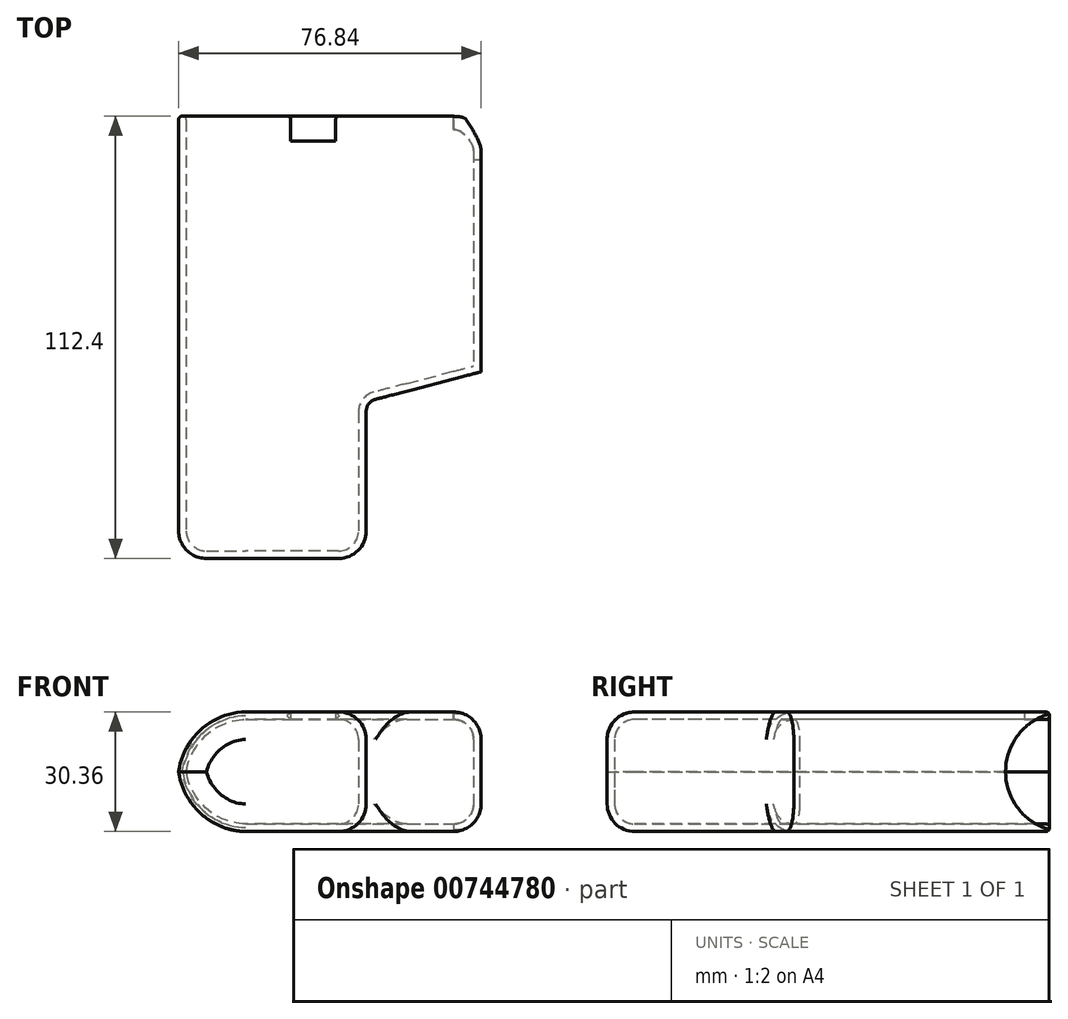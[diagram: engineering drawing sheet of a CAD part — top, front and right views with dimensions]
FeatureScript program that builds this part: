
annotation { "Feature Type Name" : "Feature", "Feature Type Description" : "" }
export const myFeature = defineFeature(function(context is Context, id is Id, definition is map)
    precondition{}
    {
        {
            var Q0;
            Q0=qCreatedBy(makeId("Top.planeOp"),FACE);
            var sketch = newSketch(context, id + "F0", { "sketchPlane" : qUnion([Q0])});
            skLineSegment(sketch, "E0", {"start": v(-37.72, -82.37) * mm, "end": v(-37.72, 28.12) * mm});
            skLineSegment(sketch, "E1", {"start": v(35.43, 28.12) * mm, "end": v(35.43, -35.38) * mm});
            skLineSegment(sketch, "E2", {"start": v(6.22, -43) * mm, "end": v(6.22, -82.37) * mm});
            skLineSegment(sketch, "E3", {"start": v(6.22, -82.37) * mm, "end": v(-37.72, -82.37) * mm});
            skLineSegment(sketch, "E4", {"start": v(-37.72, 28.12) * mm, "end": v(35.43, 28.12) * mm});
            skLineSegment(sketch, "E5", {"start": v(6.22, -43) * mm, "end": v(35.43, -35.38) * mm});
            skSolve(sketch);
        }
        {
            var Q0;
            Q0=makeQuery(id+"F0.imprint","IMPRINT",FACE,{"disambiguationData":[TD([[makeQuery(id+"F0.imprint","IMPRINT",EDGE,{"derivedFrom":sQuery(id+"F0.wireOp",EDGE,"E0")}),-1.0]])]});
            extrude(context, id + "F1", {"entities" : qUnion([Q0]), "endBound" : BoundingType.SYMMETRIC, "depth" : 26.54 * mm, "offsetDistance" : 25.4 * mm});
        }
        {
            var Q0;
            Q0=makeQuery(id+"F1.opExtrude","CAP_EDGE",EDGE,{"disambiguationData":[OSD([sQuery(id+"F0.wireOp",EDGE,"E0")])],"isStart":false});
            var Q1;
            Q1=makeQuery(id+"F1.opExtrude","CAP_EDGE",EDGE,{"disambiguationData":[OSD([sQuery(id+"F0.wireOp",EDGE,"E0")])],"isStart":true});
            fillet(context, id + "F2", {"entities" : qUnion([Q0, Q1]), "radius" : 15.24 * mm, "tangentPropagation" : true, "rho" : .4, "crossSection" : FilletCrossSection.CONIC, "allowEdgeOverflow" : false});
        }
        {
            var Q0;
            Q0=makeQuery(id+"F1.opExtrude","SWEPT_FACE",FACE,{"disambiguationData":[OSD([sQuery(id+"F0.wireOp",EDGE,"E3")])]});
            var Q1;
            Q1=makeQuery(id+"F1.opExtrude","SWEPT_FACE",FACE,{"disambiguationData":[OSD([sQuery(id+"F0.wireOp",EDGE,"E2")])]});
            var Q2;
            Q2=makeQuery(id+"F1.opExtrude","CAP_EDGE",EDGE,{"disambiguationData":[OSD([sQuery(id+"F0.wireOp",EDGE,"E1")])],"isStart":true});
            var Q3;
            Q3=makeQuery(id+"F1.opExtrude","CAP_EDGE",EDGE,{"disambiguationData":[OSD([sQuery(id+"F0.wireOp",EDGE,"E1")])],"isStart":false});
            fillet(context, id + "F3", {"entities" : qUnion([Q0, Q1, Q2, Q3]), "radius" : 5.08 * mm, "tangentPropagation" : true, "allowEdgeOverflow" : false});
        }
        {
            var Q0;
            Q0=makeQuery(id+"F1.opExtrude","SWEPT_FACE",FACE,{"disambiguationData":[OSD([sQuery(id+"F0.wireOp",EDGE,"E4")])]});
            shell(context, id + "F4", {"entities" : qUnion([Q0]), "thickness" : 1.9 * mm, "oppositeDirection" : true});
        }
        {
            var Q0;
            Q0=qCreatedBy(makeId("Top.planeOp"),FACE);
            var sketch = newSketch(context, id + "F5", { "sketchPlane" : qUnion([Q0])});
            skPoint(sketch, "E6.visualSharp", {"position": v(3.48, 27.22) * mm});
            skLineSegment(sketch, "E7", {"start": v(0.38, -82.37) * mm, "end": v(0.38, 21.77) * mm, "construction": true});
            skLineSegment(sketch, "E8", {"start": v(0.38, 21.77) * mm, "end": v(-37.72, 21.77) * mm, "construction": true});
            skLineSegment(sketch, "E9.bottom", {"start": v(0.38, 37.51) * mm, "end": v(-11.05, 37.51) * mm});
            skLineSegment(sketch, "E9.top", {"start": v(0.38, 21.77) * mm, "end": v(-11.05, 21.77) * mm});
            skLineSegment(sketch, "E9.left", {"start": v(0.38, 37.51) * mm, "end": v(0.38, 21.77) * mm});
            skLineSegment(sketch, "E9.right", {"start": v(-11.05, 37.51) * mm, "end": v(-11.05, 21.77) * mm});
            skSolve(sketch);
        }
        {
            var Q0;
            Q0=qSketchRegion(id+"F5",true);
            extrude(context, id + "F6", {"entities" : qUnion([Q0]), "operationType" : NewBodyOperationType.REMOVE, "depth" : 25.4 * mm, "offsetDistance" : 25.4 * mm});
        }
        {
            var Q0;
            {var subQ5=sQuery(id+"F0.wireOp",EDGE,"E4");var subQ13=makeQuery(id+"F1.opExtrude","SWEPT_FACE",FACE,{"disambiguationData":[OSD([subQ5])]});Q0=makeQuery(id+"F6.boolean.opBoolean","SPLIT",FACE,{"disambiguationData":[TD([makeQuery(id+"F6.opExtrude","SWEPT_FACE",FACE,{"disambiguationData":[OSD([sQuery(id+"F5.wireOp",EDGE,"E9.right")])]})])],"derivedFrom":subQ13});}
            var Q1;
            {var subQ0=sQuery(id+"F0.wireOp",EDGE,"E4");var subQ10=makeQuery(id+"F1.opExtrude","SWEPT_FACE",FACE,{"disambiguationData":[OSD([subQ0])]});Q1=makeQuery(id+"F6.boolean.opBoolean","SPLIT",FACE,{"disambiguationData":[TD([makeQuery(id+"F6.opExtrude","SWEPT_FACE",FACE,{"disambiguationData":[OSD([sQuery(id+"F5.wireOp",EDGE,"E9.left")])]})])],"derivedFrom":subQ10});}
            fillet(context, id + "F7", {"entities" : qUnion([Q0, Q1]), "radius" : 0.89 * mm, "tangentPropagation" : true, "allowEdgeOverflow" : false});
        }
        {
            var Q0;
            Q0=qCreatedBy(makeId("Front.planeOp"),FACE);
            var sketch = newSketch(context, id + "F8", { "sketchPlane" : qUnion([Q0])});
            skLineSegment(sketch, "E10.bottom", {"start": v(-43.08, -19.25) * mm, "end": v(42.92, -19.25) * mm});
            skLineSegment(sketch, "E10.top", {"start": v(-43.08, 0) * mm, "end": v(42.92, 0) * mm});
            skLineSegment(sketch, "E10.left", {"start": v(-43.08, -19.25) * mm, "end": v(-43.08, 0) * mm});
            skLineSegment(sketch, "E10.right", {"start": v(42.92, -19.25) * mm, "end": v(42.92, 0) * mm});
            skSolve(sketch);
        }
        {
            var Q0;
            Q0=qCreatedBy(makeId("Right.planeOp"),FACE);
            var sketch = newSketch(context, id + "F9", { "sketchPlane" : qUnion([Q0])});
            skCircle(sketch, "E11", {"center": v(32.18, 0) * mm, "radius": 15.24 * mm});
            skSolve(sketch);
        }
        {
            var Q0;
            Q0=makeQuery(id+"F9.imprint","IMPRINT",FACE,{"disambiguationData":[TD([[makeQuery(id+"F9.imprint","IMPRINT",EDGE,{"derivedFrom":sQuery(id+"F9.wireOp",EDGE,"E11")}),1.0]])]});
            extrude(context, id + "F10", {"entities" : qUnion([Q0]), "operationType" : NewBodyOperationType.REMOVE, "depth" : 50.8 * mm, "offsetDistance" : 25.4 * mm, "hasSecondDirection" : true, "secondDirectionOppositeDirection" : false, "secondDirectionDepth" : 30.35 * mm});
        }
    });
